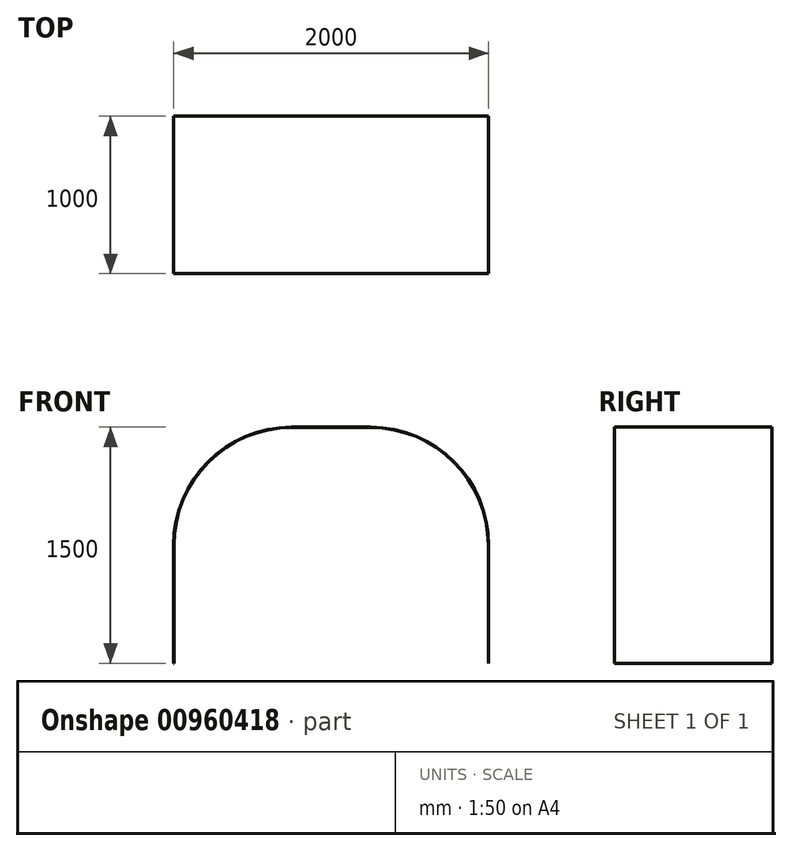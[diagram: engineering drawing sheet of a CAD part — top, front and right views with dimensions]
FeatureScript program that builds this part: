
annotation { "Feature Type Name" : "Feature", "Feature Type Description" : "" }
export const myFeature = defineFeature(function(context is Context, id is Id, definition is map)
    precondition{}
    {
        {
            var Q0;
            Q0=qCreatedBy(makeId("Front.planeOp"),FACE);
            var sketch = newSketch(context, id + "F0", { "sketchPlane" : qUnion([Q0])});
            skLineSegment(sketch, "E0.top", {"start": v(-1000, 0) * mm, "end": v(1000, 0) * mm});
            skLineSegment(sketch, "E1", {"start": v(-1000, 1500) * mm, "end": v(-1000, 0) * mm});
            skLineSegment(sketch, "E2", {"start": v(1000, 0) * mm, "end": v(1000, 1500) * mm});
            skLineSegment(sketch, "E3", {"start": v(1000, 1500) * mm, "end": v(-1000, 1500) * mm});
            skSolve(sketch);
        }
        {
            var Q0;
            Q0=makeQuery(id+"F0.imprint","IMPRINT",FACE,{"disambiguationData":[TD([[makeQuery(id+"F0.imprint","IMPRINT",EDGE,{"derivedFrom":sQuery(id+"F0.wireOp",EDGE,"E0.bottom")}),-1.0]])]});
            var Q1;
            Q1=makeQuery(id+"F0.imprint","IMPRINT",FACE,{"disambiguationData":[TD([[makeQuery(id+"F0.imprint","IMPRINT",EDGE,{"derivedFrom":sQuery(id+"F0.wireOp",EDGE,"E0.top")}),1.0]])]});
            extrude(context, id + "F1", {"entities" : qUnion([Q0, Q1]), "endBound" : BoundingType.SYMMETRIC, "depth" : 1000 * mm, "offsetDistance" : 25 * mm});
        }
        {
            var Q0;
            Q0=makeQuery(id+"F1.opExtrude","SWEPT_EDGE",EDGE,{"disambiguationData":[OSD([sQuery(id+"F0.wireOp",EDGE,"E1"),sQuery(id+"F0.wireOp",EDGE,"E3")])]});
            var Q1;
            Q1=makeQuery(id+"F1.opExtrude","SWEPT_EDGE",EDGE,{"disambiguationData":[OSD([sQuery(id+"F0.wireOp",EDGE,"E2"),sQuery(id+"F0.wireOp",EDGE,"E3")])]});
            fillet(context, id + "F2", {"entities" : qUnion([Q0, Q1]), "radius" : 750 * mm, "tangentPropagation" : true, "allowEdgeOverflow" : false});
        }
        {
            var Q0;
            Q0=makeQuery(id+"F1.opExtrude","CAP_FACE",FACE,{"disambiguationData":[OSD([sQuery(id+"F0.wireOp",EDGE,"E0.bottom"),sQuery(id+"F0.wireOp",EDGE,"E0.top"),sQuery(id+"F0.wireOp",EDGE,"E0.left"),sQuery(id+"F0.wireOp",EDGE,"E0.right")])],"isStart":false});
            var sketch = newSketch(context, id + "F3", { "sketchPlane" : qUnion([Q0])});
            skLineSegment(sketch, "E4.0", {"start": v(-998, 750) * mm, "end": v(-998, -0.57) * mm});
            skLineSegment(sketch, "E4.1", {"start": v(998, -0.57) * mm, "end": v(998, 750) * mm});
            skArc(sketch, "E4.2", {"start": v(998, 750) * mm, "mid": v(778.92, 1278.92) * mm, "end": v(250, 1498) * mm});
            skLineSegment(sketch, "E4.3", {"start": v(250, 1498) * mm, "end": v(-250, 1498) * mm});
            skArc(sketch, "E4.4", {"start": v(-250, 1498) * mm, "mid": v(-778.92, 1278.92) * mm, "end": v(-998, 750) * mm});
            skLineSegment(sketch, "E5", {"start": v(-998, -0.57) * mm, "end": v(998, -0.57) * mm});
            skSolve(sketch);
        }
        {
            var Q0;
            Q0=qSketchRegion(id+"F3",true);
            extrude(context, id + "F4", {"entities" : qUnion([Q0]), "operationType" : NewBodyOperationType.REMOVE, "endBound" : BoundingType.THROUGH_ALL, "oppositeDirection" : true, "depth" : 25 * mm, "offsetDistance" : 25 * mm});
        }
    });
